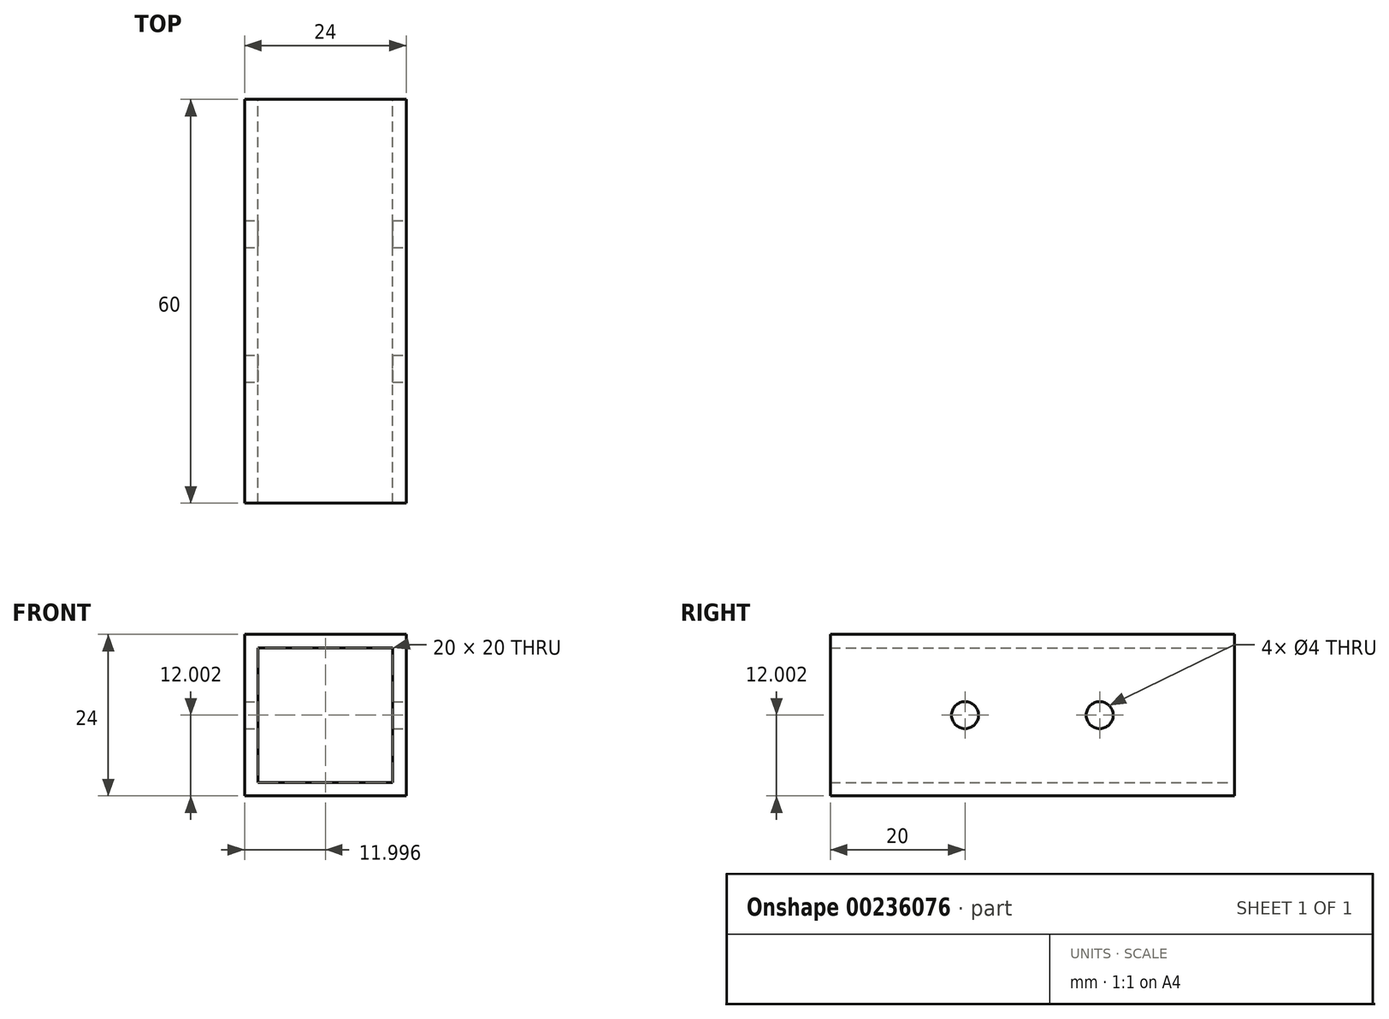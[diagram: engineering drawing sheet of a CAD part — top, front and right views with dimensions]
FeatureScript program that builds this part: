
annotation { "Feature Type Name" : "Feature", "Feature Type Description" : "" }
export const myFeature = defineFeature(function(context is Context, id is Id, definition is map)
    precondition{}
    {
        {
            var Q0;
            Q0=qCreatedBy(makeId("Front.planeOp"),FACE);
            var sketch = newSketch(context, id + "F0", { "sketchPlane" : qUnion([Q0])});
            skLineSegment(sketch, "E0.bottom", {"start": v(-14.67, -0.75) * mm, "end": v(5.33, -0.75) * mm});
            skLineSegment(sketch, "E0.top", {"start": v(-14.67, -20.75) * mm, "end": v(5.33, -20.75) * mm});
            skLineSegment(sketch, "E0.left", {"start": v(-14.67, -0.75) * mm, "end": v(-14.67, -20.75) * mm});
            skLineSegment(sketch, "E0.right", {"start": v(5.33, -0.75) * mm, "end": v(5.33, -20.75) * mm});
            skLineSegment(sketch, "E1.bottom", {"start": v(-16.67, -22.75) * mm, "end": v(7.33, -22.75) * mm});
            skLineSegment(sketch, "E1.top", {"start": v(-16.67, 1.25) * mm, "end": v(7.33, 1.25) * mm});
            skLineSegment(sketch, "E1.left", {"start": v(-16.67, -22.75) * mm, "end": v(-16.67, 1.25) * mm});
            skLineSegment(sketch, "E1.right", {"start": v(7.33, -22.75) * mm, "end": v(7.33, 1.25) * mm});
            skSolve(sketch);
        }
        {
            var Q0;
            Q0=makeQuery(id+"F0.imprint","IMPRINT",FACE,{"disambiguationData":[TD([[makeQuery(id+"F0.imprint","IMPRINT",EDGE,{"derivedFrom":sQuery(id+"F0.wireOp",EDGE,"E0.bottom")}),1.0]])]});
            extrude(context, id + "F1", {"entities" : qUnion([Q0]), "depth" : 60 * mm});
        }
        {
            var Q0;
            Q0=makeQuery(id+"F1.opExtrude","SWEPT_FACE",FACE,{"disambiguationData":[OSD([sQuery(id+"F0.wireOp",EDGE,"E1.right")])]});
            var sketch = newSketch(context, id + "F2", { "sketchPlane" : qUnion([Q0])});
            skCircle(sketch, "E2", {"center": v(-40, -10.75) * mm, "radius": 2 * mm});
            skCircle(sketch, "E3", {"center": v(-20, -10.75) * mm, "radius": 2 * mm});
            skPoint(sketch, "E4", {"position": v(-60, -10.75) * mm});
            skPoint(sketch, "E5", {"position": v(0, -10.75) * mm});
            skSolve(sketch);
        }
        {
            var Q0;
            Q0=makeQuery(id+"F2.imprint","IMPRINT",FACE,{"disambiguationData":[TD([[makeQuery(id+"F2.imprint","IMPRINT",EDGE,{"derivedFrom":sQuery(id+"F2.wireOp",EDGE,"E2")}),1.0]])]});
            var Q1;
            Q1=makeQuery(id+"F2.imprint","IMPRINT",FACE,{"disambiguationData":[TD([[makeQuery(id+"F2.imprint","IMPRINT",EDGE,{"derivedFrom":sQuery(id+"F2.wireOp",EDGE,"E3")}),1.0]])]});
            extrude(context, id + "F3", {"entities" : qUnion([Q0, Q1]), "operationType" : NewBodyOperationType.REMOVE, "oppositeDirection" : true, "depth" : 25 * mm});
        }
    });
